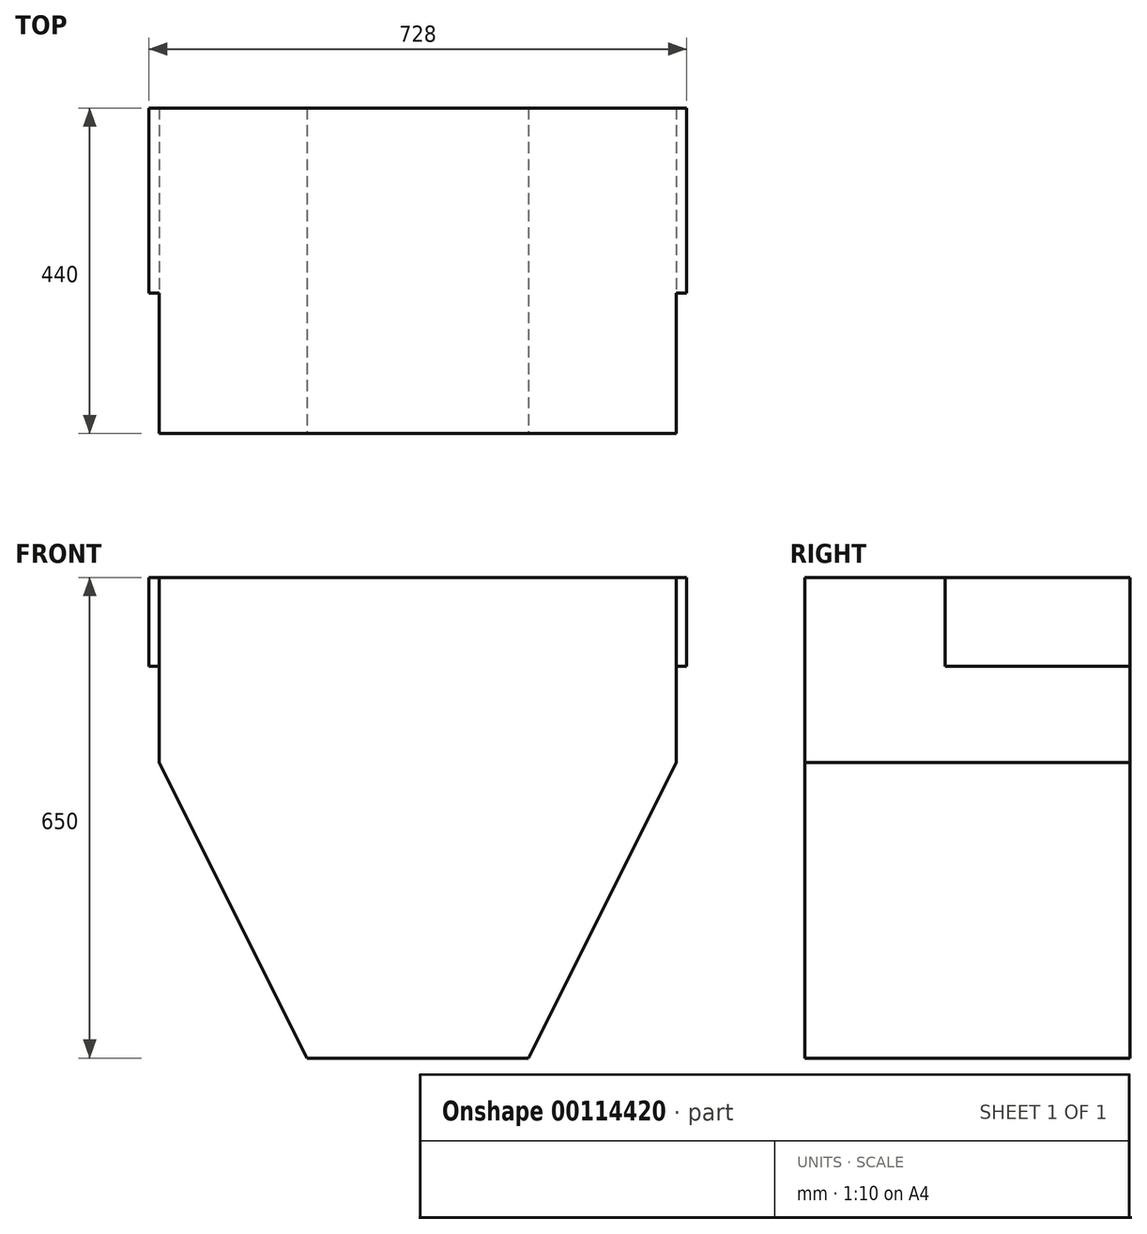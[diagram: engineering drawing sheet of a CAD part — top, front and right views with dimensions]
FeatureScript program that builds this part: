
annotation { "Feature Type Name" : "Feature", "Feature Type Description" : "" }
export const myFeature = defineFeature(function(context is Context, id is Id, definition is map)
    precondition{}
    {
        {
            var Q0;
            Q0=qCreatedBy(makeId("Front.planeOp"),FACE);
            var sketch = newSketch(context, id + "F0", { "sketchPlane" : qUnion([Q0])});
            skLineSegment(sketch, "E0.bottom", {"start": v(350, 325) * mm, "end": v(-350, 325) * mm});
            skLineSegment(sketch, "E0.top", {"start": v(350, -325) * mm, "end": v(-350, -325) * mm});
            skLineSegment(sketch, "E0.left", {"start": v(350, 325) * mm, "end": v(350, -325) * mm});
            skLineSegment(sketch, "E0.right", {"start": v(-350, 325) * mm, "end": v(-350, -325) * mm});
            skPoint(sketch, "E0.middle", {"position": v(0, 0) * mm});
            skSolve(sketch);
        }
        {
            var Q0;
            Q0 = qSketchRegion(id + "F0", true);
            extrude(context, id + "F1", {"entities" : qUnion([Q0]), "depth" : 440 * mm});
        }
        {
            var Q0;
            Q0=makeQuery(id+"F1.opExtrude","CAP_FACE",FACE,{"disambiguationData":[OSD([sQuery(id+"F0.wireOp",EDGE,"E0.bottom"),sQuery(id+"F0.wireOp",EDGE,"E0.top"),sQuery(id+"F0.wireOp",EDGE,"E0.left"),sQuery(id+"F0.wireOp",EDGE,"E0.right")])],"isStart":false});
            var sketch = newSketch(context, id + "F2", { "sketchPlane" : qUnion([Q0])});
            skLineSegment(sketch, "E1", {"start": v(-350, 75) * mm, "end": v(-150, -325) * mm});
            skLineSegment(sketch, "E2", {"start": v(-150, -325) * mm, "end": v(-350, -325) * mm});
            skLineSegment(sketch, "E3", {"start": v(-350, -325) * mm, "end": v(-350, 75) * mm});
            skLineSegment(sketch, "E4", {"start": v(150, -325) * mm, "end": v(350, 75) * mm});
            skLineSegment(sketch, "E5", {"start": v(350, 75) * mm, "end": v(350, -325) * mm});
            skLineSegment(sketch, "E6", {"start": v(350, -325) * mm, "end": v(150, -325) * mm});
            skSolve(sketch);
        }
        {
            var Q0;
            Q0 = qSketchRegion(id + "F2", true);
            extrude(context, id + "F3", {"entities" : qUnion([Q0]), "operationType" : NewBodyOperationType.REMOVE, "endBound" : BoundingType.THROUGH_ALL, "oppositeDirection" : true, "depth" : 25 * mm});
        }
        {
            var Q0;
            Q0=makeQuery(id+"F1.opExtrude","SWEPT_FACE",FACE,{"disambiguationData":[OSD([sQuery(id+"F0.wireOp",EDGE,"E0.right")])]});
            var sketch = newSketch(context, id + "F4", { "sketchPlane" : qUnion([Q0])});
            skLineSegment(sketch, "E7.bottom", {"start": v(0, 325) * mm, "end": v(250, 325) * mm});
            skLineSegment(sketch, "E7.top", {"start": v(0, 205) * mm, "end": v(250, 205) * mm});
            skLineSegment(sketch, "E7.left", {"start": v(0, 325) * mm, "end": v(0, 205) * mm});
            skLineSegment(sketch, "E7.right", {"start": v(250, 325) * mm, "end": v(250, 205) * mm});
            skSolve(sketch);
        }
        {
            var Q0;
            Q0 = qSketchRegion(id + "F4", true);
            extrude(context, id + "F5", {"entities" : qUnion([Q0]), "operationType" : NewBodyOperationType.ADD, "depth" : ((98 - 70) / 2) * mm});
        }
        {
            var Q0;
            Q0=makeQuery(id+"F1.opExtrude","SWEPT_FACE",FACE,{"disambiguationData":[OSD([sQuery(id+"F0.wireOp",EDGE,"E0.left")])]});
            var sketch = newSketch(context, id + "F6", { "sketchPlane" : qUnion([Q0])});
            skLineSegment(sketch, "E8.bottom", {"start": v(0, 325) * mm, "end": v(-250, 325) * mm});
            skLineSegment(sketch, "E8.top", {"start": v(0, 205) * mm, "end": v(-250, 205) * mm});
            skLineSegment(sketch, "E8.left", {"start": v(0, 325) * mm, "end": v(0, 205) * mm});
            skLineSegment(sketch, "E8.right", {"start": v(-250, 325) * mm, "end": v(-250, 205) * mm});
            skSolve(sketch);
        }
        {
            var Q0;
            Q0 = qSketchRegion(id + "F6", true);
            extrude(context, id + "F7", {"entities" : qUnion([Q0]), "operationType" : NewBodyOperationType.ADD, "depth" : ((98 - 70) / 2) * mm});
        }
    });
